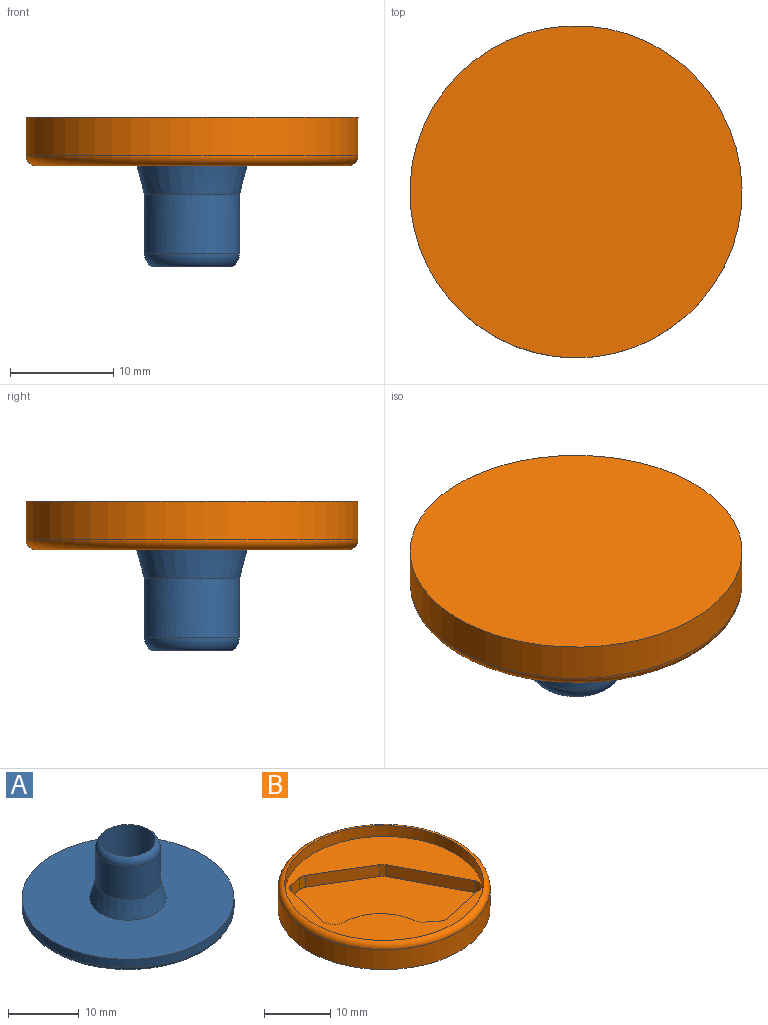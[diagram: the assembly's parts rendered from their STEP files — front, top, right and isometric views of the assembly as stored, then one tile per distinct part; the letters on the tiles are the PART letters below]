
ASSEMBLY  parts=2 mates=1
PART A: 8 faces, bbox 32.5x32.5x12.2 mm
  f0: plane 29x29mm, normal (0,0,-1), area 612.9mm2, adj f1,f6
  f1: torus R=14.5mm, axis (0,0,-1), area 73.1mm2, adj f0,f2
  f2: cylinder r=15mm len=30mm, axis (0,0,-1), area 141.4mm2, adj f1,f3
  f3: plane 30x30mm, normal (0,0,1), area 615.2mm2, adj f2,f4
  f4: cone r=4.6mm half-angle=14.9deg, axis (0,0,-1), area 97.5mm2, adj f3,f5
  f5: cylinder r=4.6mm len=9.2mm, axis (0,0,-1), area 165.5mm2, adj f4,f7
  f6: cylinder r=3.89mm len=12mm, axis (0,0,1), area 293.5mm2, adj f0,f7
  f7: torus R=3.1mm, axis (0,0,1), area 41.6mm2, adj f5,f6
PART B: 20 faces, bbox 34.7x34.7x4.7 mm
  f0: plane 30.1x30.1mm, normal (0,0,1), area 395.7mm2, adj f1,f2,f3,f4,f5,f6,f7,f8
  f1: cylinder r=1.5mm len=2.2mm, axis (0,0,-1), area 2.4mm2, adj f0,f2,f14,f19
  f2: plane 9.89x5.93mm, normal (-0.51,-0.86,0), area 25.4mm2, adj f0,f1,f3,f19
  f3: cylinder r=2mm len=2.2mm, axis (0,0,-1), area 2.4mm2, adj f0,f2,f4,f19
  f4: plane 12.39x6.49mm, normal (-0.89,-0.46,0), area 30.8mm2, adj f0,f3,f5,f19
  f5: cylinder r=1.5mm len=2.2mm, axis (0,0,-1), area 6.1mm2, adj f0,f4,f6,f19
  f6: plane 8.93x2.2mm, normal (-0.21,0.98,0), area 20.1mm2, adj f0,f5,f7,f19
  f7: cylinder r=1.5mm len=2.2mm, axis (0,0,-1), area 2.9mm2, adj f0,f6,f8,f19
  f8: plane 2.2x1.62mm, normal (0.62,0.78,0), area 4.6mm2, adj f0,f7,f9,f19
  f9: cylinder r=2.35mm len=2.2mm, axis (0,0,-1), area 4.6mm2, adj f0,f8,f10,f19
  f10: cylinder r=7.97mm len=7.8mm, axis (0,0,-1), area 25.3mm2, adj f0,f9,f11,f19
  f11: cylinder r=2.38mm len=2.98mm, axis (0,0,-1), area 9.2mm2, adj f0,f10,f12,f19
  f12: plane 8.5x2.23mm, normal (0.97,-0.25,0), area 19.3mm2, adj f0,f11,f13,f19
  f13: cylinder r=1.5mm len=2.2mm, axis (0,0,-1), area 3.7mm2, adj f0,f12,f14,f19
  f14: plane 2.22x2.2mm, normal (0.2,-0.98,0), area 5mm2, adj f0,f1,f13,f19
  f15: cylinder r=16.05mm len=32.1mm, axis (0,0,-1), area 373.1mm2, adj f16,f18
  f16: plane 32.1x32.1mm, normal (0,0,-1), area 809.3mm2, adj f15
  f17: cylinder r=15.05mm len=30.1mm, axis (0,0,-1), area 189.1mm2, adj f0,f18
  f18: torus R=15.05mm, axis (0,0,1), area 154.8mm2, adj f15,f17
  f19: plane 24.04x23.43mm, normal (0,0,1), area 315.9mm2, adj f1,f2,f3,f4,f5,f6,f7,f8
PLACE A rot(axis=(0.2,-0.98,0),180deg) t=(-14.89,-4.94,-3.44)mm
PLACE B rot(axis=(-0.98,-0.2,0),180deg) t=(-14.89,-4.94,-0.99)mm
MATE revolute A.f1 <-> B.f15  axis (0,0,1) through (-14.89,-4.94,-4.69)mm
